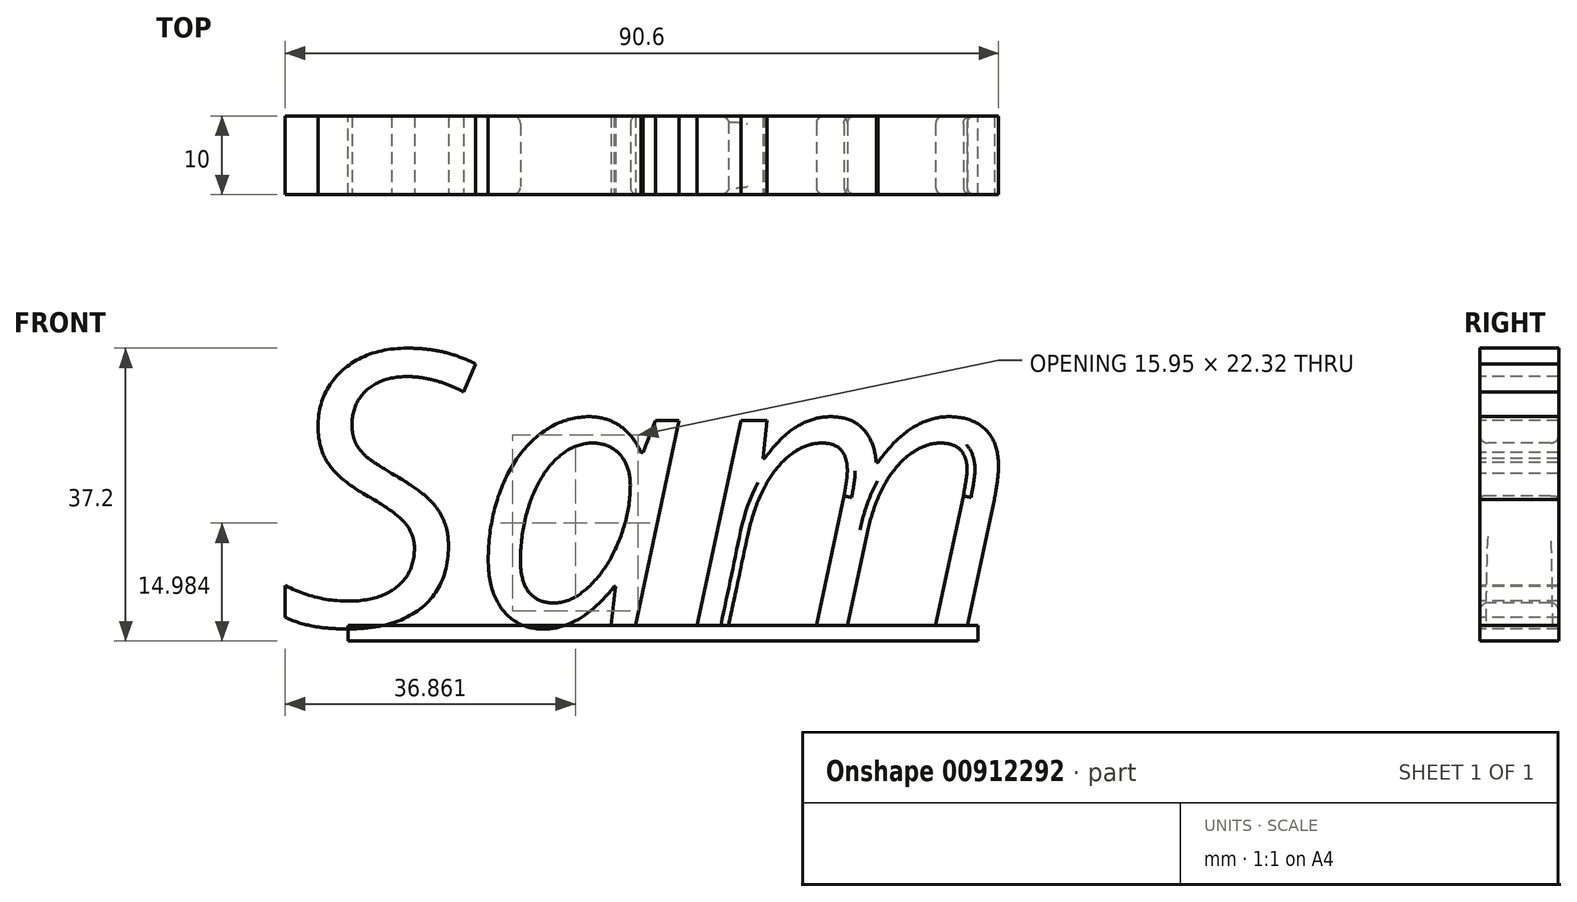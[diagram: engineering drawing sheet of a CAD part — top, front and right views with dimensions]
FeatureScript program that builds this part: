
annotation { "Feature Type Name" : "Feature", "Feature Type Description" : "" }
export const myFeature = defineFeature(function(context is Context, id is Id, definition is map)
    precondition{}
    {
        {
            var Q0;
            Q0=qCreatedBy(makeId("Front.planeOp"),FACE);
            var sketch = newSketch(context, id + "F0", { "sketchPlane" : qUnion([Q0])});
            skText(sketch, "E0", { "text": "Sam", "fontName": "OpenSans-Italic.ttf"});
            const initialGuessF0  = {"E0": [-0.04734, 0, 1, 0, 0.035]};
            skSetInitialGuess(sketch, initialGuessF0);
            skSolve(sketch);
        }
        {
            var Q0;
            Q0 = qSketchRegion(id + "F0", true);
            extrude(context, id + "F1", {"entities" : qUnion([Q0]), "endBound" : BoundingType.SYMMETRIC, "oppositeDirection" : true, "depth" : 10 * mm, "offsetDistance" : 25 * mm});
        }
        {
            var Q0;
            Q0=qCreatedBy(makeId("Front.planeOp"),FACE);
            var sketch = newSketch(context, id + "F2", { "sketchPlane" : qUnion([Q0])});
            skLineSegment(sketch, "E1.bottom", {"start": v(-38.4, 0) * mm, "end": v(41.6, 0) * mm});
            skLineSegment(sketch, "E1.top", {"start": v(-38.4, -2) * mm, "end": v(41.6, -2) * mm});
            skLineSegment(sketch, "E1.left", {"start": v(-38.4, 0) * mm, "end": v(-38.4, -2) * mm});
            skLineSegment(sketch, "E1.right", {"start": v(41.6, 0) * mm, "end": v(41.6, -2) * mm});
            skSolve(sketch);
        }
        {
            var Q0;
            Q0 = qSketchRegion(id + "F2", true);
            extrude(context, id + "F3", {"entities" : qUnion([Q0]), "endBound" : BoundingType.SYMMETRIC, "depth" : 10 * mm, "offsetDistance" : 25 * mm});
        }
        {
            var Q0;
            Q0=makeQuery(id+"F1.opExtrude","CAP_EDGE",EDGE,{"disambiguationData":[OSD([sQuery(id+"F0.wireOp",EDGE,"E0.sketch_text.stroke-48")])],"isStart":true});
            var Q1;
            Q1=makeQuery(id+"F1.opExtrude","CAP_EDGE",EDGE,{"disambiguationData":[OSD([sQuery(id+"F0.wireOp",EDGE,"E0.sketch_text.stroke-58")])],"isStart":true});
            var Q2;
            Q2=makeQuery(id+"F1.opExtrude","CAP_EDGE",EDGE,{"disambiguationData":[OSD([sQuery(id+"F0.wireOp",EDGE,"E0.sketch_text.stroke-83")])],"isStart":true});
            var Q3;
            Q3=makeQuery(id+"F1.opExtrude","CAP_EDGE",EDGE,{"disambiguationData":[OSD([sQuery(id+"F0.wireOp",EDGE,"E0.sketch_text.stroke-58")])],"isStart":false});
            var Q4;
            Q4=makeQuery(id+"F1.opExtrude","CAP_EDGE",EDGE,{"disambiguationData":[OSD([sQuery(id+"F0.wireOp",EDGE,"E0.sketch_text.stroke-48")])],"isStart":false});
            var Q5;
            Q5=makeQuery(id+"F1.opExtrude","CAP_EDGE",EDGE,{"disambiguationData":[OSD([sQuery(id+"F0.wireOp",EDGE,"E0.sketch_text.stroke-83")])],"isStart":false});
            fillet(context, id + "F4", {"entities" : qUnion([Q0, Q1, Q2, Q3, Q4, Q5]), "radius" : 1 * mm, "tangentPropagation" : true, "allowEdgeOverflow" : false});
        }
    });
